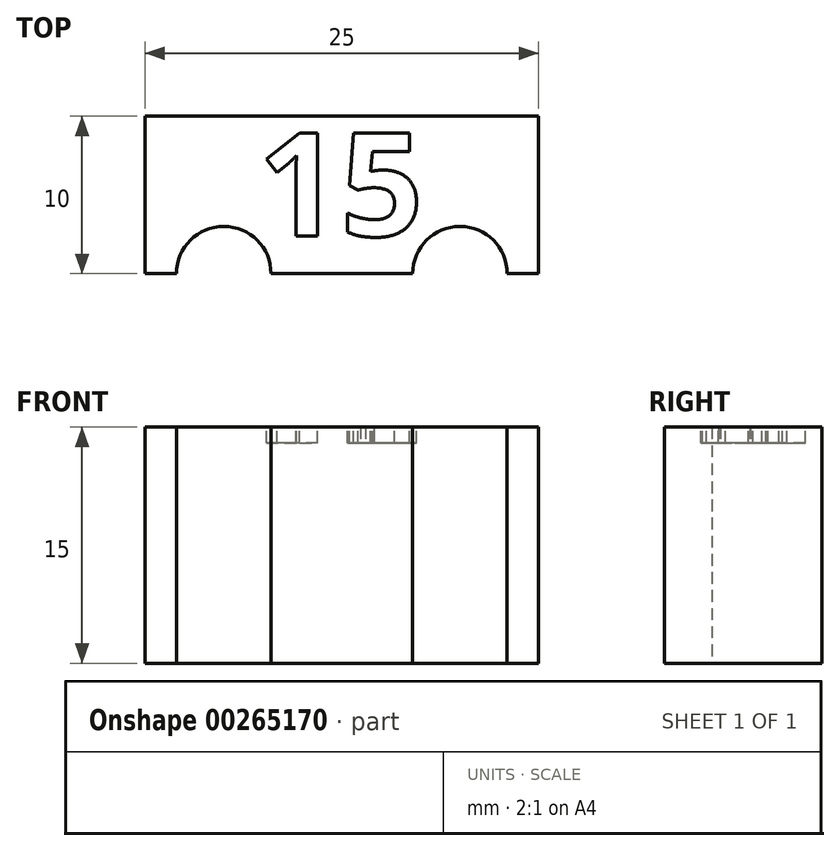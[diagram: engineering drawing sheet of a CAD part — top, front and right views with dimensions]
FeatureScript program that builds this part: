
annotation { "Feature Type Name" : "Feature", "Feature Type Description" : "" }
export const myFeature = defineFeature(function(context is Context, id is Id, definition is map)
    precondition{}
    {
        {
            var Q0;
            Q0=qCreatedBy(makeId("Top.planeOp"),FACE);
            var sketch = newSketch(context, id + "F0", { "sketchPlane" : qUnion([Q0])});
            skLineSegment(sketch, "E0.bottom", {"start": v(12.5, 5) * mm, "end": v(-12.5, 5) * mm});
            skLineSegment(sketch, "E0.top", {"start": v(12.5, -5) * mm, "end": v(-12.5, -5) * mm});
            skLineSegment(sketch, "E0.left", {"start": v(12.5, 5) * mm, "end": v(12.5, -5) * mm});
            skLineSegment(sketch, "E0.right", {"start": v(-12.5, 5) * mm, "end": v(-12.5, -5) * mm});
            skPoint(sketch, "E0.middle", {"position": v(0, 0) * mm});
            skSolve(sketch);
        }
        {
            var Q0;
            Q0=qSketchRegion(id+"F0",true);
            extrude(context, id + "F1", {"entities" : qUnion([Q0]), "depth" : 15 * mm});
        }
        {
            var Q0;
            Q0=qCreatedBy(makeId("Top.planeOp"),FACE);
            var sketch = newSketch(context, id + "F2", { "sketchPlane" : qUnion([Q0])});
            skCircle(sketch, "E1", {"center": v(-7.5, -5) * mm, "radius": 3 * mm});
            skCircle(sketch, "E2", {"center": v(7.5, -5) * mm, "radius": 3 * mm});
            skSolve(sketch);
        }
        {
            var Q0;
            Q0=qSketchRegion(id+"F2",true);
            extrude(context, id + "F3", {"entities" : qUnion([Q0]), "operationType" : NewBodyOperationType.REMOVE, "endBound" : BoundingType.THROUGH_ALL, "depth" : 25 * mm});
        }
        {
            var Q0;
            Q0=makeQuery(id+"F1.opExtrude","CAP_FACE",FACE,{"disambiguationData":[OSD([sQuery(id+"F0.wireOp",EDGE,"E0.bottom"),sQuery(id+"F0.wireOp",EDGE,"E0.top"),sQuery(id+"F0.wireOp",EDGE,"E0.left"),sQuery(id+"F0.wireOp",EDGE,"E0.right")])],"isStart":false});
            var sketch = newSketch(context, id + "F4", { "sketchPlane" : qUnion([Q0])});
            skLineSegment(sketch, "E3", {"start": v(0, 4) * mm, "end": v(0, 5) * mm, "construction": true});
            skText(sketch, "E4", { "text": "15", "fontName": "OpenSans-Bold.ttf"});
            const initialGuessF4  = {"E4": [-0.00533, -0.00261, 1, 0, 0.00661]};
            skSetInitialGuess(sketch, initialGuessF4);
            skSolve(sketch);
        }
        {
            var Q0;
            Q0 = qSketchRegion(id + "F4", true);
            extrude(context, id + "F5", {"entities" : qUnion([Q0]), "operationType" : NewBodyOperationType.REMOVE, "oppositeDirection" : true, "depth" : 1 * mm});
        }
    });
